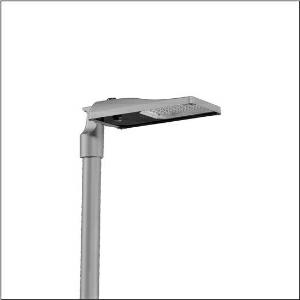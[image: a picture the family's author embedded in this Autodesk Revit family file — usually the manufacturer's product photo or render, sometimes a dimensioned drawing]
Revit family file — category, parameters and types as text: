
# Revit family: streetlight_sl_31_mini___st0_8a_5xh6c31t08ja_3bb2
name_source: partatom
category: Lighting Fixtures
units: mm (PartAtom-declared; Revit-internal decimal feet)

## family parameters
Cut with Voids When Loaded = No
Host = Face
Light Source = No
Part Type = Normal
Room Calculation Point = No
Round Connector Dimension = Use Diameter
Shared = No

## types (1)
- --- (1 x LED, 12270 lm, 82.5 W, 3000K)
    Apparent Load = 83 VA
    CIE Flux Codes = 41 75 97 100 100
    Color Rendering = 70
    Color Temperature = 3000K
    Default Elevation = 1800 mm
    Description = Streetlight SL 31 mini D4i, Desk-Remote mast luminaire for post-top, side-entry; light control with lens of PMMA; light distribution: ST0.8a, direct asymmetric distribution, for standard-compliant lighting for roads and squares; LED: luminous flux: 12.270lm, light colour: 730, colour temperature: 3000K; luminous efficacy: 148,7lm/W; control: pre-setting: logarithmic dimming characteristic, flexible luminous flux parameterisation, time-dependent luminous flux control, constant luminous flux control, power reduction, intelligent temperature release in ECG and LED module, overheat protection; luminaire housing, of diecast aluminium, SITECO metallic grey (DB 702S), corrosivity category C5 high according to DIN EN ISO 12944; cover of toughened safety glass, transparent, opened without tools; mast flange of diecast aluminium, SITECO metallic grey (DB 702S), spigot size: 76/60mm, mast flange included unmounted; with cable H07RN-F 2x 1.5mm², cable length: 10,5m, connection cable pre-assembled; mains connection: 220..240V, AC, 50/60Hz; power consumption (at start of service life): 82,5W / (at end of service life): 90,1W / (with reduced operation 50%): 36,8W; protection rating (complete): IP66; insulation class (complete): insulation class II (safety insulation); impact resistance: IK09; certification: CE, ENEC, ENEC+, VDE, UKCA, ZD4i; permissible operating ambient temperature for outdoor applications: -40..+50°C; packaging unit: 1 piece

Light Distribution: ST0.8a
    Height = 76 mm
    Lamp = 1 x LED
    Lamp Light Flux = 12270 lm
    Lamp Power = 82.5 W
    Lamp count = 1
    Length = 547 mm
    Luminous efficacy = 149 lm/W
    Manufacturer = Siteco
    ModVariant = No
    Model = 5XH6C31T08JA
    Number of Poles = 1
    OnlyDefault = Yes
    Power Factor = 1
    Product Name = Streetlight SL 31 mini | ST0.8a
    Product group = mast luminaire | pylon top
    ProductGroupID = 6100
    Protection Class = Protection class II
    Protection Degree = IP 66
    RLX_Detail_Level = 1
    RLX_Emergency_Light_Flux = 0 lm
    RLX_Emergency_Type = 0
    RLX_Emergency_Type_DB = No
    RlxData = <blob elided: 40005 chars, md5=370d617b>
    Socket = socket
    Standby Power = 0 W
    System Light Flux = 12270 lm
    System Power = 83 W
    Type Comments = factory setting: luminous flux: 100 % | dim-lin: 254 | 870 mA
    Type Image = l_1300332.jpg
    URL = http://relux.com
    VarID = @adj_056449
    Voltage = 0 V
    Weight = 0.00 kg
    Width = 265 mm

## geometry (parser evidence)
native form markers: Blend x4, Sweep x10
no freeform markers — native parametric forms only
